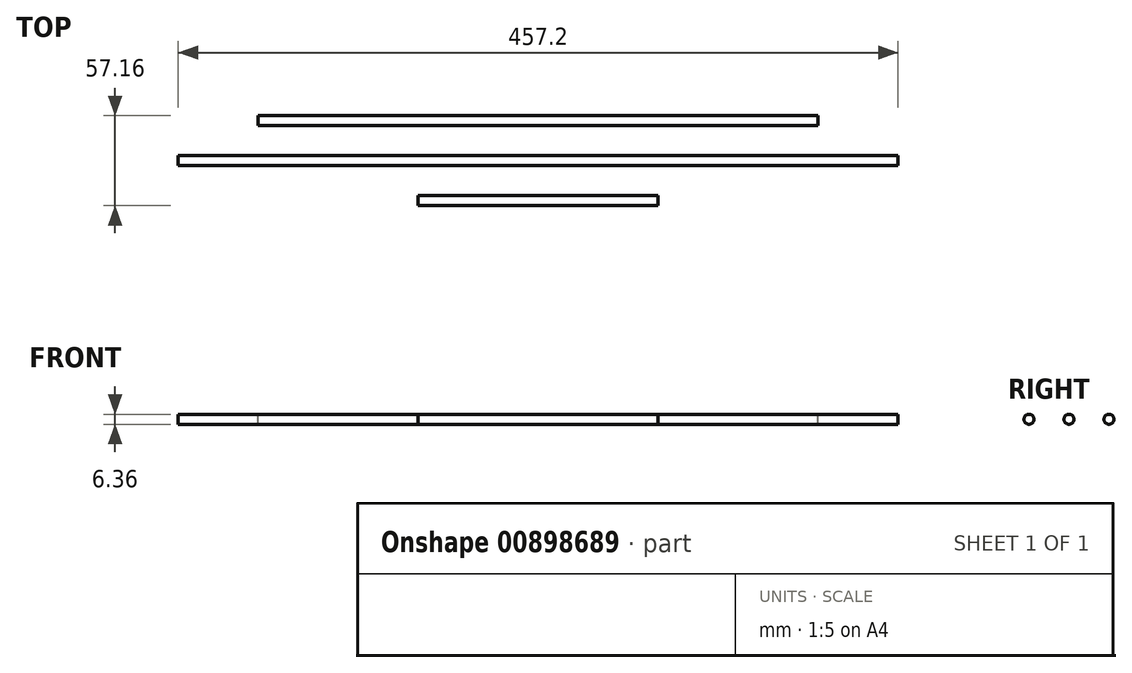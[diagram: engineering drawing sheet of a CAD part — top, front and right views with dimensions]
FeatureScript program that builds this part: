
annotation { "Feature Type Name" : "Feature", "Feature Type Description" : "" }
export const myFeature = defineFeature(function(context is Context, id is Id, definition is map)
    precondition{}
    {
        {
            var Q0;
            Q0=qCreatedBy(makeId("Right.planeOp"),FACE);
            var sketch = newSketch(context, id + "F0", { "sketchPlane" : qUnion([Q0])});
            skCircle(sketch, "E0", {"center": v(0, 0) * mm, "radius": 3.17 * mm});
            skSolve(sketch);
        }
        {
            var Q0;
            Q0=makeQuery(id+"F0.imprint","IMPRINT",FACE,{"disambiguationData":[TD([[makeQuery(id+"F0.imprint","IMPRINT",EDGE,{"derivedFrom":sQuery(id+"F0.wireOp",EDGE,"E0")}),1.0]])]});
            extrude(context, id + "F1", {"entities" : qUnion([Q0]), "depth" : 355.6 * mm, "offsetDistance" : 25.4 * mm, "symmetric" : true});
        }
        {
            var Q0;
            Q0=qCreatedBy(makeId("Right.planeOp"),FACE);
            var sketch = newSketch(context, id + "F2", { "sketchPlane" : qUnion([Q0])});
            skCircle(sketch, "E1", {"center": v(-25.4, 0) * mm, "radius": 3.18 * mm});
            skLineSegment(sketch, "E2", {"start": v(0, 0) * mm, "end": v(-25.4, 0) * mm, "construction": true});
            skSolve(sketch);
        }
        {
            var Q0;
            Q0=makeQuery(id+"F2.imprint","IMPRINT",FACE,{"disambiguationData":[TD([[makeQuery(id+"F2.imprint","IMPRINT",EDGE,{"derivedFrom":sQuery(id+"F2.wireOp",EDGE,"E1")}),1.0]])]});
            extrude(context, id + "F3", {"entities" : qUnion([Q0]), "depth" : 457.2 * mm, "offsetDistance" : 25.4 * mm, "symmetric" : true});
        }
        {
            var Q0;
            Q0=qCreatedBy(makeId("Right.planeOp"),FACE);
            var sketch = newSketch(context, id + "F4", { "sketchPlane" : qUnion([Q0])});
            skCircle(sketch, "E3", {"center": v(-50.8, 0) * mm, "radius": 3.17 * mm});
            skSolve(sketch);
        }
        {
            var Q0;
            Q0=makeQuery(id+"F4.imprint","IMPRINT",FACE,{"disambiguationData":[TD([[makeQuery(id+"F4.imprint","IMPRINT",EDGE,{"derivedFrom":sQuery(id+"F4.wireOp",EDGE,"E3")}),1.0]])]});
            extrude(context, id + "F5", {"entities" : qUnion([Q0]), "depth" : 152.4 * mm, "offsetDistance" : 25.4 * mm, "symmetric" : true});
        }
    });
